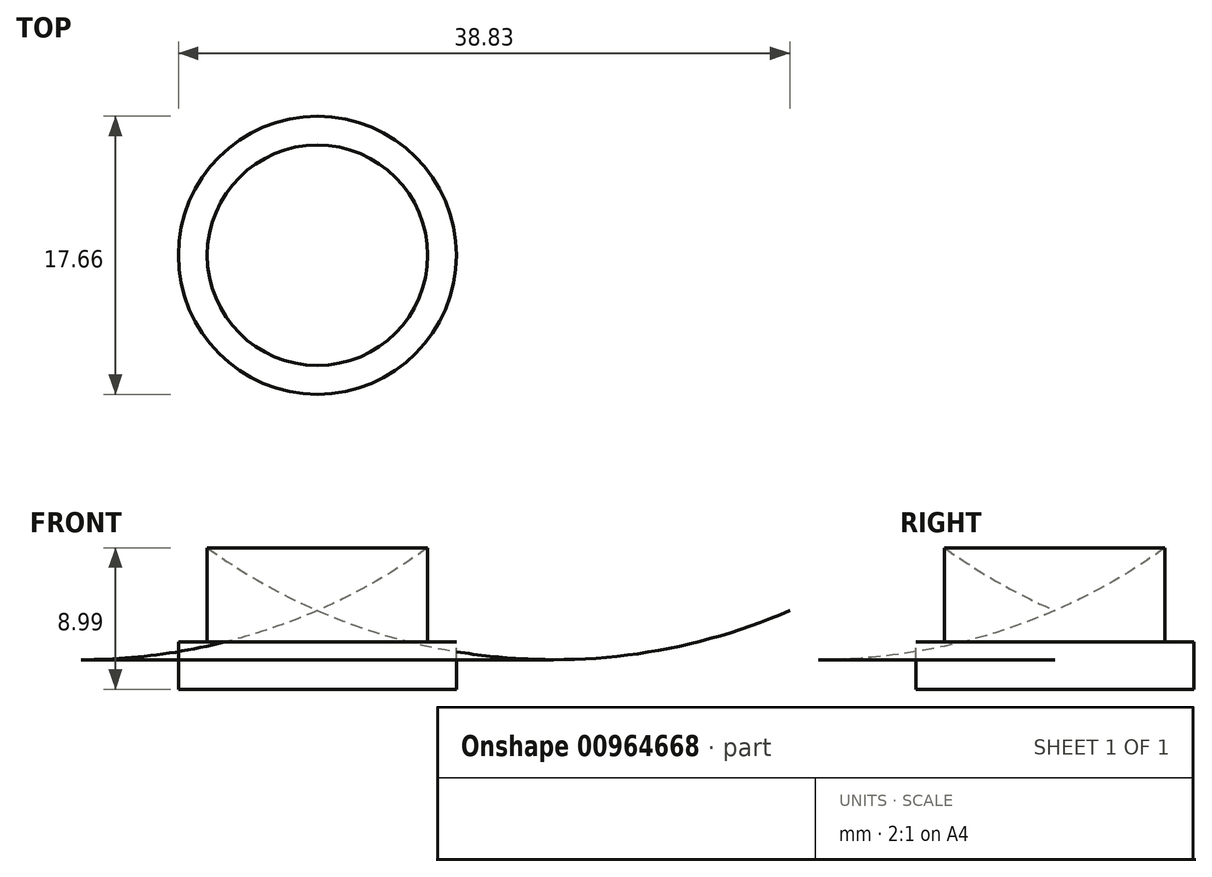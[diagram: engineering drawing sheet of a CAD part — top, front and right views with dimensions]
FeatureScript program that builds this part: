
annotation { "Feature Type Name" : "Feature", "Feature Type Description" : "" }
export const myFeature = defineFeature(function(context is Context, id is Id, definition is map)
    precondition{}
    {
        {
            var Q0;
            Q0=qCreatedBy(makeId("Front.planeOp"),FACE);
            var sketch = newSketch(context, id + "F0", { "sketchPlane" : qUnion([Q0])});
            skLineSegment(sketch, "E0", {"start": v(-56.8, 0) * mm, "end": v(-56.8, 6) * mm});
            skLineSegment(sketch, "E1", {"start": v(-49.8, 2) * mm, "end": v(-49.8, 0) * mm});
            skLineSegment(sketch, "E2", {"start": v(-49.8, 0) * mm, "end": v(-56.8, 0) * mm});
            skArc(sketch, "E3", {"start": v(-56.8, 5.99) * mm, "mid": v(-53.4, 3.8) * mm, "end": v(-49.8, 2) * mm});
            skLineSegment(sketch, "E4", {"start": v(-49.8, 2) * mm, "end": v(-56.8, 2) * mm, "construction": true});
            skLineSegment(sketch, "E5", {"start": v(-56.8, 6) * mm, "end": v(-56.8, 2) * mm, "construction": true});
            skSolve(sketch);
        }
        {
            var Q0;
            Q0=makeQuery(id+"F0.imprint","IMPRINT",FACE,{"disambiguationData":[TD([[makeQuery(id+"F0.imprint","IMPRINT",EDGE,{"derivedFrom":sQuery(id+"F0.wireOp",EDGE,"E1")}),-1.0]])]});
            var Q1;
            Q1=sQuery(id+"F0.wireOp",EDGE,"E1");
            revolve(context, id + "F1", {"surfaceOperationType" : NewSurfaceOperationType.NEW, "entities" : qUnion([Q0]), "axis" : qUnion([Q1]), "revolveType" : RevolveType.FULL});
        }
        {
            var Q0;
            Q0=makeQuery(id+"F1.opRevolve","SWEPT_FACE",FACE,{"disambiguationData":[OSD([sQuery(id+"F0.wireOp",EDGE,"E2")])]});
            var sketch = newSketch(context, id + "F2", { "sketchPlane" : qUnion([Q0])});
            skCircle(sketch, "E6", {"center": v(-49.8, 0) * mm, "radius": 8.83 * mm});
            skSolve(sketch);
        }
        {
            var Q0;
            Q0=makeQuery(id+"F2.imprint","IMPRINT",FACE,{"disambiguationData":[TD([[makeQuery(id+"F2.imprint","IMPRINT",EDGE,{"derivedFrom":makeQuery(id+"F1.opRevolve","SWEPT_EDGE",EDGE,{"disambiguationData":[OSD([sQuery(id+"F0.wireOp",EDGE,"E0"),sQuery(id+"F0.wireOp",EDGE,"E2")])]})}),-1.0]])]});
            var Q1;
            Q1=makeQuery(id+"F2.imprint","IMPRINT",FACE,{"disambiguationData":[TD([[makeQuery(id+"F2.imprint","IMPRINT",EDGE,{"derivedFrom":sQuery(id+"F2.wireOp",EDGE,"E6")}),1.0]])]});
            extrude(context, id + "F3", {"entities" : qUnion([Q0, Q1]), "operationType" : NewBodyOperationType.ADD, "depth" : 3 * mm, "offsetDistance" : 25 * mm});
        }
    });
